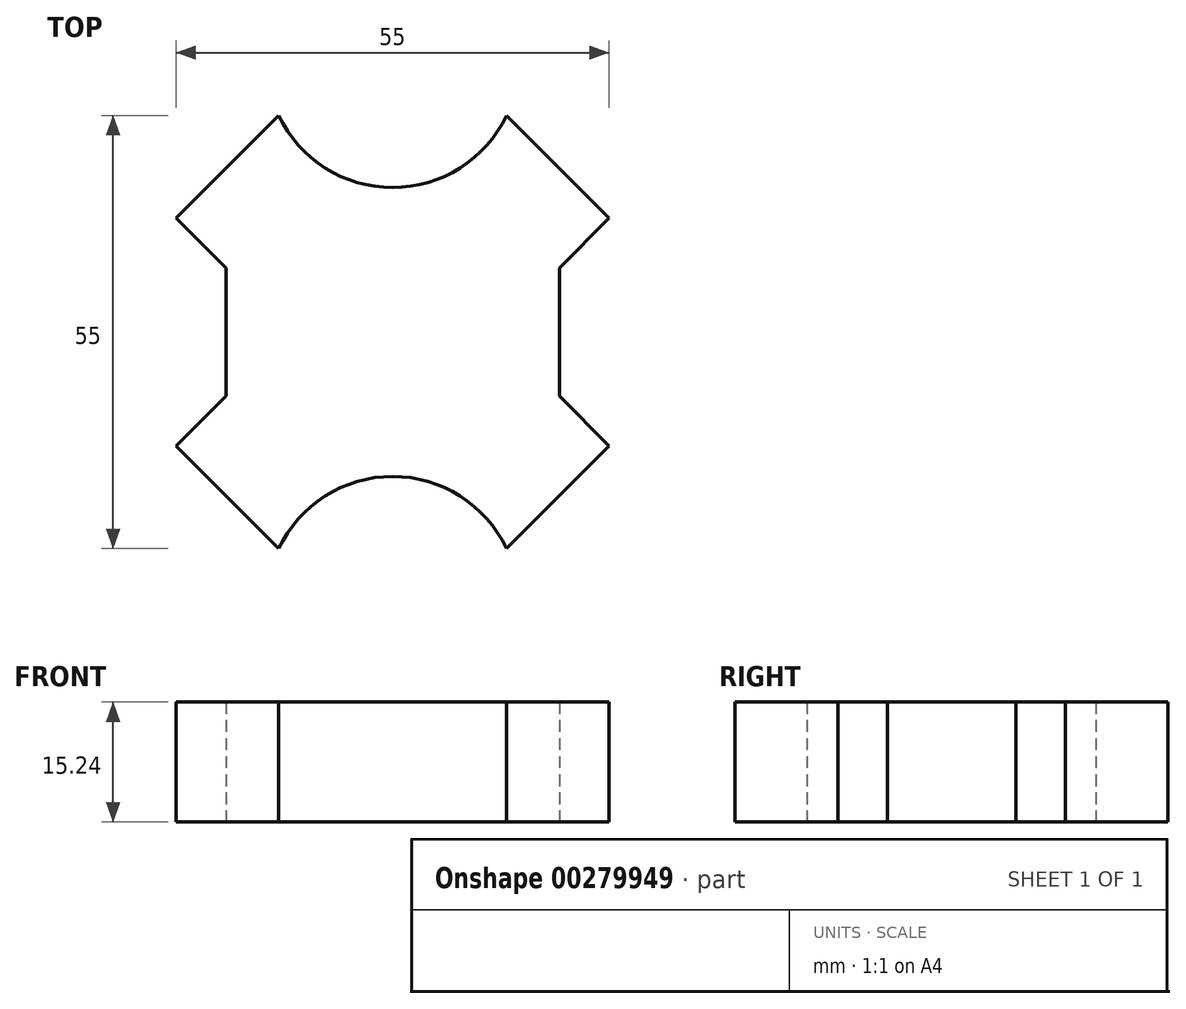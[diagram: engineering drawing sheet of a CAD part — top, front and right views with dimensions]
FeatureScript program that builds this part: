
annotation { "Feature Type Name" : "Feature", "Feature Type Description" : "" }
export const myFeature = defineFeature(function(context is Context, id is Id, definition is map)
    precondition{}
    {
        {
            var Q0;
            Q0=qCreatedBy(makeId("Top.planeOp"),FACE);
            var sketch = newSketch(context, id + "F0", { "sketchPlane" : qUnion([Q0])});
            skLineSegment(sketch, "E0.bottom", {"start": v(-27.5, 27.5) * mm, "end": v(27.5, 27.5) * mm});
            skLineSegment(sketch, "E0.top", {"start": v(-27.5, -27.5) * mm, "end": v(27.5, -27.5) * mm});
            skLineSegment(sketch, "E0.left", {"start": v(-27.5, 27.5) * mm, "end": v(-27.5, -27.5) * mm});
            skLineSegment(sketch, "E0.right", {"start": v(27.5, 27.5) * mm, "end": v(27.5, -27.5) * mm});
            skPoint(sketch, "E0.middle", {"position": v(0, 0) * mm});
            skLineSegment(sketch, "E1", {"start": v(-27.5, 14.46) * mm, "end": v(-14.46, 27.5) * mm});
            skLineSegment(sketch, "E2", {"start": v(-14.46, -27.5) * mm, "end": v(-27.5, -14.46) * mm});
            skLineSegment(sketch, "E3", {"start": v(27.5, -14.46) * mm, "end": v(14.46, -27.5) * mm});
            skLineSegment(sketch, "E4", {"start": v(14.46, 27.5) * mm, "end": v(27.5, 14.46) * mm});
            skLineSegment(sketch, "E5", {"start": v(-27.5, -14.46) * mm, "end": v(14.46, 27.5) * mm});
            skLineSegment(sketch, "E6", {"start": v(27.5, 14.46) * mm, "end": v(-14.46, -27.5) * mm});
            skLineSegment(sketch, "E7", {"start": v(14.46, -27.5) * mm, "end": v(-27.5, 14.46) * mm});
            skLineSegment(sketch, "E8", {"start": v(-14.46, 27.5) * mm, "end": v(27.5, -14.46) * mm});
            skLineSegment(sketch, "E9", {"start": v(-21.19, 8.15) * mm, "end": v(-21.19, -8.15) * mm});
            skPoint(sketch, "E10.startSnap0", {"position": v(-6.52, -6.52) * mm});
            skLineSegment(sketch, "E11", {"start": v(21.19, 8.15) * mm, "end": v(21.19, -8.15) * mm});
            skLineSegment(sketch, "E12", {"start": v(0, 0) * mm, "end": v(0, 19.5) * mm});
            skLineSegment(sketch, "E13", {"start": v(0, 0) * mm, "end": v(0, -19.5) * mm});
            skArc(sketch, "E14", {"start": v(-14.46, 27.5) * mm, "mid": v(0, 18.35) * mm, "end": v(14.46, 27.5) * mm});
            skArc(sketch, "E15", {"start": v(14.46, -27.5) * mm, "mid": v(0, -18.35) * mm, "end": v(-14.46, -27.5) * mm});
            skSolve(sketch);
        }
        {
            var Q0;
            {var subQ1=sQuery(id+"F0.wireOp",EDGE,"E1");Q0=makeQuery(id+"F0.imprint","IMPRINT",FACE,{"disambiguationData":[TD([[makeQuery(id+"F0.imprint","IMPRINT",EDGE,{"derivedFrom":subQ1}),-1.0]])]});}
            var Q1;
            {var subQ0=sQuery(id+"F0.wireOp",EDGE,"E9");Q1=makeQuery(id+"F0.imprint","IMPRINT",FACE,{"disambiguationData":[TD([[makeQuery(id+"F0.imprint","IMPRINT",EDGE,{"derivedFrom":subQ0}),1.0]])]});}
            var Q2;
            {var subQ0=sQuery(id+"F0.wireOp",EDGE,"icapobU0-kjJc-5MZK-hCs5-2VOc3pI1r2Eq");var subQ3=sQuery(id+"F0.wireOp",EDGE,"E13");var subQ5=makeQuery(id+"F0.imprint","INTERSECT",VERTEX,{"derivedFrom":[subQ3,subQ0]});Q2=makeQuery(id+"F0.imprint","IMPRINT",FACE,{"disambiguationData":[TD([[makeQuery(id+"F0.imprint","IMPRINT",EDGE,{"disambiguationData":[TD([[subQ5,-1.0]])],"derivedFrom":subQ0}),-1.0]])]});}
            var Q3;
            {var subQ8=sQuery(id+"F0.wireOp",EDGE,"E3");Q3=makeQuery(id+"F0.imprint","IMPRINT",FACE,{"disambiguationData":[TD([[makeQuery(id+"F0.imprint","IMPRINT",EDGE,{"derivedFrom":subQ8}),-1.0]])]});}
            var Q4;
            {var subQ0=sQuery(id+"F0.wireOp",EDGE,"E8");var subQ1=sQuery(id+"F0.wireOp",EDGE,"E6");var subQ2=makeQuery(id+"F0.imprint","INTERSECT",VERTEX,{"derivedFrom":[subQ1,subQ0]});Q4=makeQuery(id+"F0.imprint","IMPRINT",FACE,{"disambiguationData":[TD([[makeQuery(id+"F0.imprint","IMPRINT",EDGE,{"disambiguationData":[TD([[subQ2,-1.0]])],"derivedFrom":subQ1}),-1.0]])]});}
            var Q5;
            {var subQ0=sQuery(id+"F0.wireOp",EDGE,"dU5gtBeY-orIi-1e0j-SJ68-1lr1gswzRo5k");var subQ3=sQuery(id+"F0.wireOp",EDGE,"E12");var subQ5=makeQuery(id+"F0.imprint","INTERSECT",VERTEX,{"derivedFrom":[subQ3,subQ0]});Q5=makeQuery(id+"F0.imprint","IMPRINT",FACE,{"disambiguationData":[TD([[makeQuery(id+"F0.imprint","IMPRINT",EDGE,{"disambiguationData":[TD([[subQ5,1.0]])],"derivedFrom":subQ0}),-1.0]])]});}
            var Q6;
            {var subQ0=sQuery(id+"F0.wireOp",EDGE,"dU5gtBeY-orIi-1e0j-SJ68-1lr1gswzRo5k");var subQ3=sQuery(id+"F0.wireOp",EDGE,"E12");var subQ5=makeQuery(id+"F0.imprint","INTERSECT",VERTEX,{"derivedFrom":[subQ3,subQ0]});Q6=makeQuery(id+"F0.imprint","IMPRINT",FACE,{"disambiguationData":[TD([[makeQuery(id+"F0.imprint","IMPRINT",EDGE,{"disambiguationData":[TD([[subQ5,-1.0]])],"derivedFrom":subQ0}),-1.0]])]});}
            var Q7;
            {var subQ0=sQuery(id+"F0.wireOp",EDGE,"E7");var subQ1=sQuery(id+"F0.wireOp",EDGE,"E5");var subQ2=makeQuery(id+"F0.imprint","INTERSECT",VERTEX,{"derivedFrom":[subQ1,subQ0]});Q7=makeQuery(id+"F0.imprint","IMPRINT",FACE,{"disambiguationData":[TD([[makeQuery(id+"F0.imprint","IMPRINT",EDGE,{"disambiguationData":[TD([[subQ2,-1.0]])],"derivedFrom":subQ1}),-1.0]])]});}
            var Q8;
            {var subQ6=sQuery(id+"F0.wireOp",EDGE,"E4");Q8=makeQuery(id+"F0.imprint","IMPRINT",FACE,{"disambiguationData":[TD([[makeQuery(id+"F0.imprint","IMPRINT",EDGE,{"derivedFrom":subQ6}),-1.0]])]});}
            var Q9;
            {var subQ0=sQuery(id+"F0.wireOp",EDGE,"icapobU0-kjJc-5MZK-hCs5-2VOc3pI1r2Eq");var subQ3=sQuery(id+"F0.wireOp",EDGE,"E13");var subQ5=makeQuery(id+"F0.imprint","INTERSECT",VERTEX,{"derivedFrom":[subQ3,subQ0]});Q9=makeQuery(id+"F0.imprint","IMPRINT",FACE,{"disambiguationData":[TD([[makeQuery(id+"F0.imprint","IMPRINT",EDGE,{"disambiguationData":[TD([[subQ5,1.0]])],"derivedFrom":subQ0}),-1.0]])]});}
            var Q10;
            {var subQ0=sQuery(id+"F0.wireOp",EDGE,"E11");Q10=makeQuery(id+"F0.imprint","IMPRINT",FACE,{"disambiguationData":[TD([[makeQuery(id+"F0.imprint","IMPRINT",EDGE,{"derivedFrom":subQ0}),-1.0]])]});}
            var Q11;
            {var subQ0=sQuery(id+"F0.wireOp",EDGE,"E15");var subQ1=sQuery(id+"F0.wireOp",EDGE,"E6");var subQ2=makeQuery(id+"F0.imprint","INTERSECT",VERTEX,{"derivedFrom":[subQ1,subQ0]});Q11=makeQuery(id+"F0.imprint","IMPRINT",FACE,{"disambiguationData":[TD([[makeQuery(id+"F0.imprint","IMPRINT",EDGE,{"disambiguationData":[TD([[subQ2,1.0]])],"derivedFrom":subQ0}),-1.0]])]});}
            var Q12;
            {var subQ0=sQuery(id+"F0.wireOp",EDGE,"E14");var subQ1=sQuery(id+"F0.wireOp",EDGE,"E5");var subQ2=makeQuery(id+"F0.imprint","INTERSECT",VERTEX,{"derivedFrom":[subQ1,subQ0]});Q12=makeQuery(id+"F0.imprint","IMPRINT",FACE,{"disambiguationData":[TD([[makeQuery(id+"F0.imprint","IMPRINT",EDGE,{"disambiguationData":[TD([[subQ2,1.0]])],"derivedFrom":subQ0}),-1.0]])]});}
            var Q13;
            {var subQ0=sQuery(id+"F0.wireOp",EDGE,"E14");var subQ3=sQuery(id+"F0.wireOp",EDGE,"E12");var subQ5=makeQuery(id+"F0.imprint","INTERSECT",VERTEX,{"derivedFrom":[subQ3,subQ0]});Q13=makeQuery(id+"F0.imprint","IMPRINT",FACE,{"disambiguationData":[TD([[makeQuery(id+"F0.imprint","IMPRINT",EDGE,{"disambiguationData":[TD([[subQ5,1.0]])],"derivedFrom":subQ0}),-1.0]])]});}
            var Q14;
            {var subQ0=sQuery(id+"F0.wireOp",EDGE,"E15");var subQ3=sQuery(id+"F0.wireOp",EDGE,"E13");var subQ5=makeQuery(id+"F0.imprint","INTERSECT",VERTEX,{"derivedFrom":[subQ3,subQ0]});Q14=makeQuery(id+"F0.imprint","IMPRINT",FACE,{"disambiguationData":[TD([[makeQuery(id+"F0.imprint","IMPRINT",EDGE,{"disambiguationData":[TD([[subQ5,1.0]])],"derivedFrom":subQ0}),-1.0]])]});}
            var Q15;
            {var subQ5=sQuery(id+"F0.wireOp",EDGE,"E2");Q15=makeQuery(id+"F0.imprint","IMPRINT",FACE,{"disambiguationData":[TD([[makeQuery(id+"F0.imprint","IMPRINT",EDGE,{"derivedFrom":subQ5}),-1.0]])]});}
            extrude(context, id + "F1", {"entities" : qUnion([Q0, Q1, Q2, Q3, Q4, Q5, Q6, Q7, Q8, Q9, Q10, Q11, Q12, Q13, Q14, Q15]), "depth" : 15.24 * mm});
        }
    });
